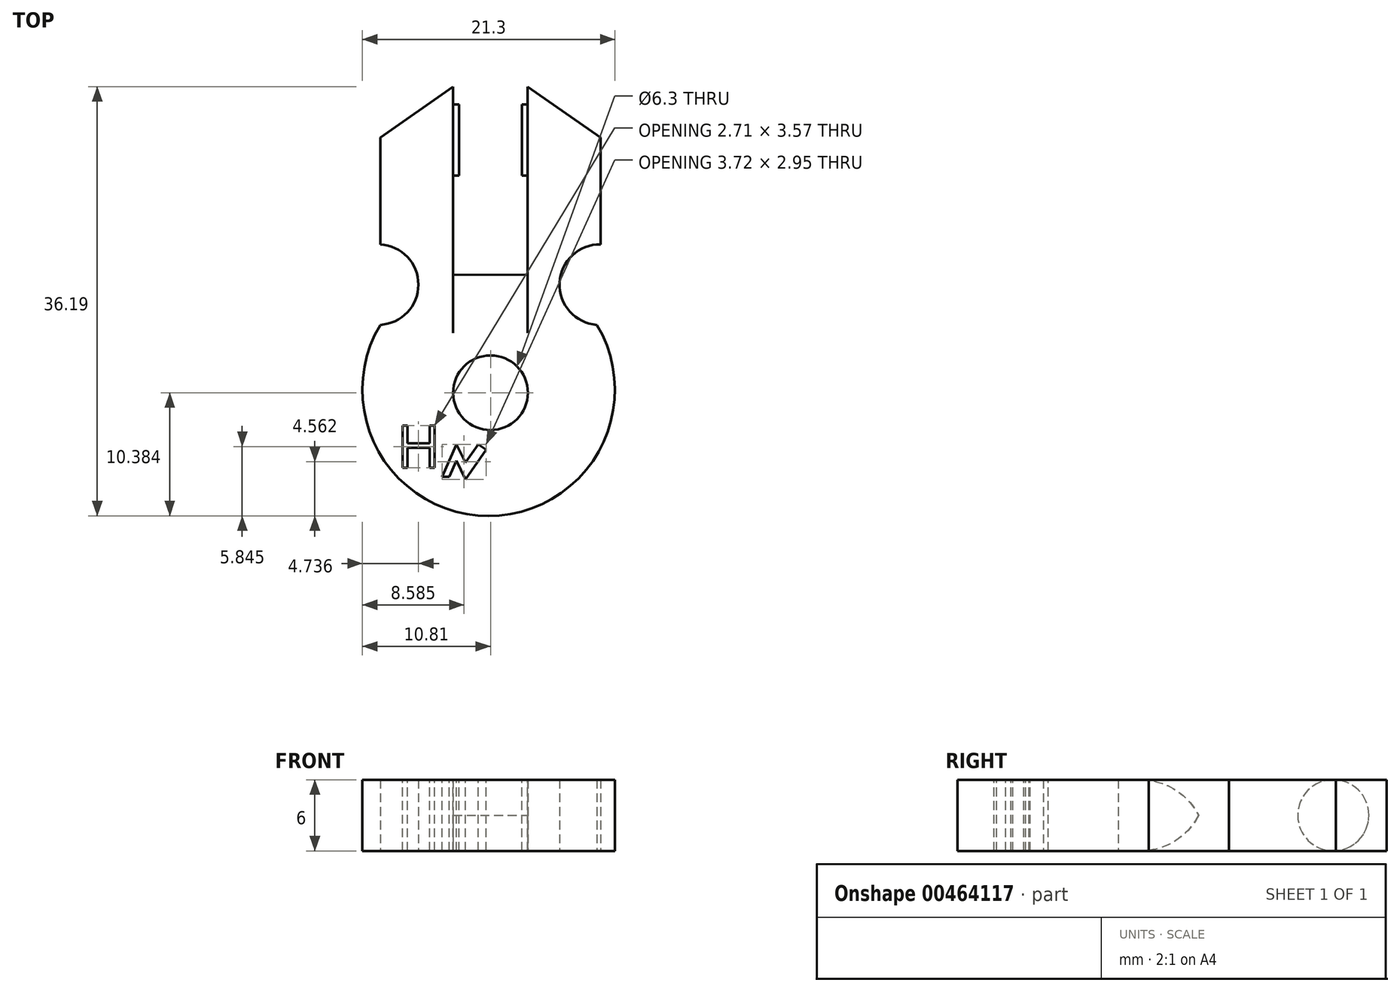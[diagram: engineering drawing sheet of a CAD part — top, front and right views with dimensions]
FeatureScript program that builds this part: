
annotation { "Feature Type Name" : "Feature", "Feature Type Description" : "" }
export const myFeature = defineFeature(function(context is Context, id is Id, definition is map)
    precondition{}
    {
        {
            var Q0;
            Q0=qCreatedBy(makeId("Top.planeOp"),FACE);
            var sketch = newSketch(context, id + "F0", { "sketchPlane" : qUnion([Q0])});
            skCircle(sketch, "E0", {"center": v(0, -31.52) * mm, "radius": 3.15 * mm});
            skLineSegment(sketch, "E1", {"start": v(3.13, -20.96) * mm, "end": v(3.13, -5.71) * mm});
            skLineSegment(sketch, "E2", {"start": v(-3.15, -20.98) * mm, "end": v(-3.15, -5.71) * mm});
            skLineSegment(sketch, "E3", {"start": v(-3.15, -5.71) * mm, "end": v(-9.3, -10) * mm});
            skLineSegment(sketch, "E4", {"start": v(-9.3, -10) * mm, "end": v(-9.3, -19) * mm});
            skArc(sketch, "E5", {"start": v(-9.3, -25.8) * mm, "mid": v(-6.08, -22.4) * mm, "end": v(-9.3, -19) * mm});
            skArc(sketch, "E6.trimOffspring", {"start": v(-9.3, -25.8) * mm, "mid": v(-0.16, -41.9) * mm, "end": v(8.98, -25.8) * mm});
            skLineSegment(sketch, "E7", {"start": v(3.13, -5.71) * mm, "end": v(9.29, -10) * mm});
            skLineSegment(sketch, "E8", {"start": v(9.29, -10) * mm, "end": v(9.29, -19) * mm});
            skArc(sketch, "E9", {"start": v(9.29, -19) * mm, "mid": v(5.83, -22.25) * mm, "end": v(8.98, -25.8) * mm});
            skLineSegment(sketch, "E10", {"start": v(-3.15, -5.71) * mm, "end": v(-3.15, -7.21) * mm});
            skLineSegment(sketch, "E11", {"start": v(-3.15, -7.21) * mm, "end": v(-2.65, -7.21) * mm});
            skLineSegment(sketch, "E12", {"start": v(-2.65, -7.21) * mm, "end": v(-2.65, -13.21) * mm});
            skLineSegment(sketch, "E13", {"start": v(-2.65, -13.21) * mm, "end": v(-3.15, -13.21) * mm});
            skLineSegment(sketch, "E14", {"start": v(3.13, -7.21) * mm, "end": v(2.63, -7.21) * mm});
            skLineSegment(sketch, "E15", {"start": v(2.63, -7.21) * mm, "end": v(2.63, -13.34) * mm});
            skPoint(sketch, "E15.endSnap0", {"position": v(3.13, -13.34) * mm});
            skLineSegment(sketch, "E16", {"start": v(-3.15, -20.98) * mm, "end": v(3.13, -20.96) * mm});
            skLineSegment(sketch, "E17", {"start": v(2.63, -13.34) * mm, "end": v(3.13, -13.34) * mm});
            skSolve(sketch);
        }
        {
            var Q0;
            Q0=makeQuery(id+"F0.imprint","IMPRINT",FACE,{"disambiguationData":[TD([[makeQuery(id+"F0.imprint","IMPRINT",EDGE,{"derivedFrom":sQuery(id+"F0.wireOp",EDGE,"E0")}),-1.0]])]});
            var Q1;
            {var subQ1=sQuery(id+"F0.wireOp",EDGE,"E7");Q1=makeQuery(id+"F0.imprint","IMPRINT",FACE,{"disambiguationData":[TD([[makeQuery(id+"F0.imprint","IMPRINT",EDGE,{"derivedFrom":subQ1}),-1.0]])]});}
            extrude(context, id + "F1", {"entities" : qUnion([Q0, Q1]), "depth" : 6 * mm});
        }
        {
            var Q0;
            Q0=makeQuery(id+"F1.opExtrude","CAP_EDGE",EDGE,{"disambiguationData":[OSD([sQuery(id+"F0.wireOp",EDGE,"E16")])],"isStart":false});
            var Q1;
            Q1=makeQuery(id+"F1.opExtrude","CAP_EDGE",EDGE,{"disambiguationData":[OSD([sQuery(id+"F0.wireOp",EDGE,"E16")])],"isStart":true});
            fillet(context, id + "F2", {"entities" : qUnion([Q0, Q1]), "radius" : 5.5 * mm, "tangentPropagation" : true, "allowEdgeOverflow" : false});
        }
        {
            var Q0;
            Q0=makeQuery(id+"F1.opExtrude","SWEPT_FACE",FACE,{"disambiguationData":[OSD([sQuery(id+"F0.wireOp",EDGE,"E2"),sQuery(id+"F0.wireOp",EDGE,"E10")])]});
            var sketch = newSketch(context, id + "F3", { "sketchPlane" : qUnion([Q0])});
            skLineSegment(sketch, "E18", {"start": v(-5.71, 3) * mm, "end": v(-7.21, 3) * mm});
            skPoint(sketch, "E18.endSnap0", {"position": v(-5.71, 3) * mm});
            skLineSegment(sketch, "E19", {"start": v(-7.21, 3) * mm, "end": v(-10.21, 3) * mm});
            skCircle(sketch, "E20", {"center": v(-10.21, 3) * mm, "radius": 3 * mm});
            skSolve(sketch);
        }
        {
            var Q0;
            Q0=qSketchRegion(id+"F3",true);
            extrude(context, id + "F4", {"entities" : qUnion([Q0]), "operationType" : NewBodyOperationType.ADD, "depth" : 7 * mm});
        }
        {
            var Q0;
            {var subQ0=makeQuery(id+"F1.opExtrude","CAP_FACE",FACE,{"disambiguationData":[OSD([sQuery(id+"F0.wireOp",EDGE,"E0"),sQuery(id+"F0.wireOp",EDGE,"lvtgTH6e-VLhN-HDL0-rTDP-TrM46i4N9T96"),sQuery(id+"F0.wireOp",EDGE,"5899688e-5abc-4eed-bafb-9ad6cdb602af0.MirrorCS"),sQuery(id+"F0.wireOp",EDGE,"E1"),sQuery(id+"F0.wireOp",EDGE,"E2"),sQuery(id+"F0.wireOp",EDGE,"E3"),sQuery(id+"F0.wireOp",EDGE,"E4"),sQuery(id+"F0.wireOp",EDGE,"E5"),sQuery(id+"F0.wireOp",EDGE,"E6.trimOffspring"),sQuery(id+"F0.wireOp",EDGE,"E7"),sQuery(id+"F0.wireOp",EDGE,"E8"),sQuery(id+"F0.wireOp",EDGE,"E9"),sQuery(id+"F0.wireOp",EDGE,"E10")])],"isStart":false});Q0=makeQuery(id+"F6DB4phLZBqyySn_1.boolean.opBoolean","MERGE",FACE,{"derivedFrom":[subQ0,makeQuery(id+"F6DB4phLZBqyySn_1.opPattern","COPY",FACE,{"derivedFrom":subQ0,"instanceName":"1"})]});}
            var sketch = newSketch(context, id + "F5", { "sketchPlane" : qUnion([Q0])});
            skLineSegment(sketch, "E21", {"start": v(-4.08, -38.59) * mm, "end": v(-2.9, -35.86) * mm});
            skLineSegment(sketch, "E22", {"start": v(-2.9, -35.86) * mm, "end": v(-2.1, -37.4) * mm});
            skLineSegment(sketch, "E23", {"start": v(-2.1, -37.4) * mm, "end": v(-1.03, -35.86) * mm});
            skLineSegment(sketch, "E24", {"start": v(-1.03, -35.86) * mm, "end": v(-0.36, -36.33) * mm});
            skLineSegment(sketch, "E25", {"start": v(-0.36, -36.33) * mm, "end": v(-2.1, -38.81) * mm});
            skLineSegment(sketch, "E26", {"start": v(-2.1, -38.81) * mm, "end": v(-2.9, -37.22) * mm});
            skPoint(sketch, "E26.endSnap0", {"position": v(-3.49, -37.22) * mm});
            skLineSegment(sketch, "E27", {"start": v(-2.9, -37.22) * mm, "end": v(-3.49, -38.59) * mm});
            skLineSegment(sketch, "E28", {"start": v(-3.49, -38.59) * mm, "end": v(-4.08, -38.59) * mm});
            skText(sketch, "E29", { "text": "H", "fontName": "OpenSans-Regular.ttf"});
            const initialGuessF5  = {"E29": [-0.00792, -0.03784, 1, 0, 0.0036]};
            skSetInitialGuess(sketch, initialGuessF5);
            skSolve(sketch);
        }
        {
            var Q0;
            Q0=qSketchRegion(id+"F5",true);
            extrude(context, id + "F6", {"entities" : qUnion([Q0]), "operationType" : NewBodyOperationType.REMOVE, "oppositeDirection" : true, "depth" : 25 * mm});
        }
        {
            var Q0;
            {var subQ0=sQuery(id+"F0.wireOp",EDGE,"E10");var subQ1=sQuery(id+"F0.wireOp",EDGE,"E2");var subQ2=makeQuery(id+"F1.opExtrude","SWEPT_FACE",FACE,{"disambiguationData":[OSD([subQ1,subQ0])]});var subQ3=sQuery(id+"F0.wireOp",EDGE,"E16");var subQ6=makeQuery(id+"F2.opFillet","BLEND_EDGE",EDGE,{"blendedFrom":[makeQuery(id+"F1.opExtrude","CAP_EDGE",EDGE,{"disambiguationData":[OSD([subQ3])],"isStart":true}),subQ2],"blendedInto":[subQ2]});Q0=makeQuery(id+"F3.imprint","IMPRINT",FACE,{"disambiguationData":[TD([[makeQuery(id+"F3.imprint","IMPRINT",EDGE,{"derivedFrom":subQ6}),1.0]])]});}
            cPlane(context, id + "F7", {"entities" : qUnion([Q0]), "cplaneType" : CPlaneType.OFFSET, "offset" : .5 * mm, "width" : 150 * mm, "height" : 150 * mm});
        }
        {
            var Q0;
            Q0=qCreatedBy(id+"F7.planeOp",FACE);
            var sketch = newSketch(context, id + "F8", { "sketchPlane" : qUnion([Q0])});
            skLineSegment(sketch, "E30.bottom", {"start": v(-6.58, 6.74) * mm, "end": v(-13.97, 6.74) * mm});
            skLineSegment(sketch, "E30.top", {"start": v(-6.58, -1.78) * mm, "end": v(-13.97, -1.78) * mm});
            skLineSegment(sketch, "E30.left", {"start": v(-6.58, 6.74) * mm, "end": v(-6.58, -1.78) * mm});
            skLineSegment(sketch, "E30.right", {"start": v(-13.97, 6.74) * mm, "end": v(-13.97, -1.78) * mm});
            skSolve(sketch);
        }
        {
            var Q0;
            Q0=makeQuery(id+"F8.imprint","IMPRINT",FACE,{"disambiguationData":[TD([[makeQuery(id+"F8.imprint","IMPRINT",EDGE,{"derivedFrom":sQuery(id+"F8.wireOp",EDGE,"E30.bottom")}),1.0]])]});
            extrude(context, id + "F9", {"entities" : qUnion([Q0]), "operationType" : NewBodyOperationType.REMOVE, "depth" : 5.3 * mm});
        }
    });
